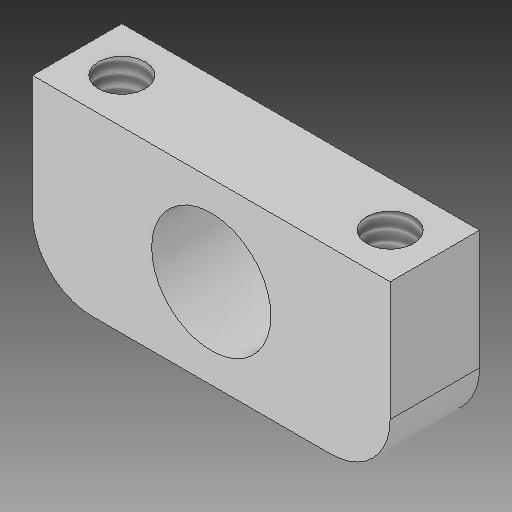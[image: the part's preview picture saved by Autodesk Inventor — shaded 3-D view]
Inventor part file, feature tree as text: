
AUTODESK INVENTOR PART (.ipt)
format: ipt  version: 2017 (Build 210142000, 142)  size: 118,784 bytes
history: native  units: in
note: dims shown in document units (in); Inventor stores cm internally (conversion verified against a paired STEP export)
features: other x3, sketch x2
ambient origin geometry x8: Origin, YZ Plane, XZ Plane, XY Plane, X Axis, Y Axis, Z Axis, Center Point
bodies: Solid1 (feature_tree)
feature tree (5):
  other  "WheelSuspensionHub.ipt"
  other  "Solid1::WheelSuspensionHub.ipt"
  other  "TaggingFeature1"
  sketch  "Sketch1"  dims[d0=0.3937in]
  sketch  "Sketch2"
